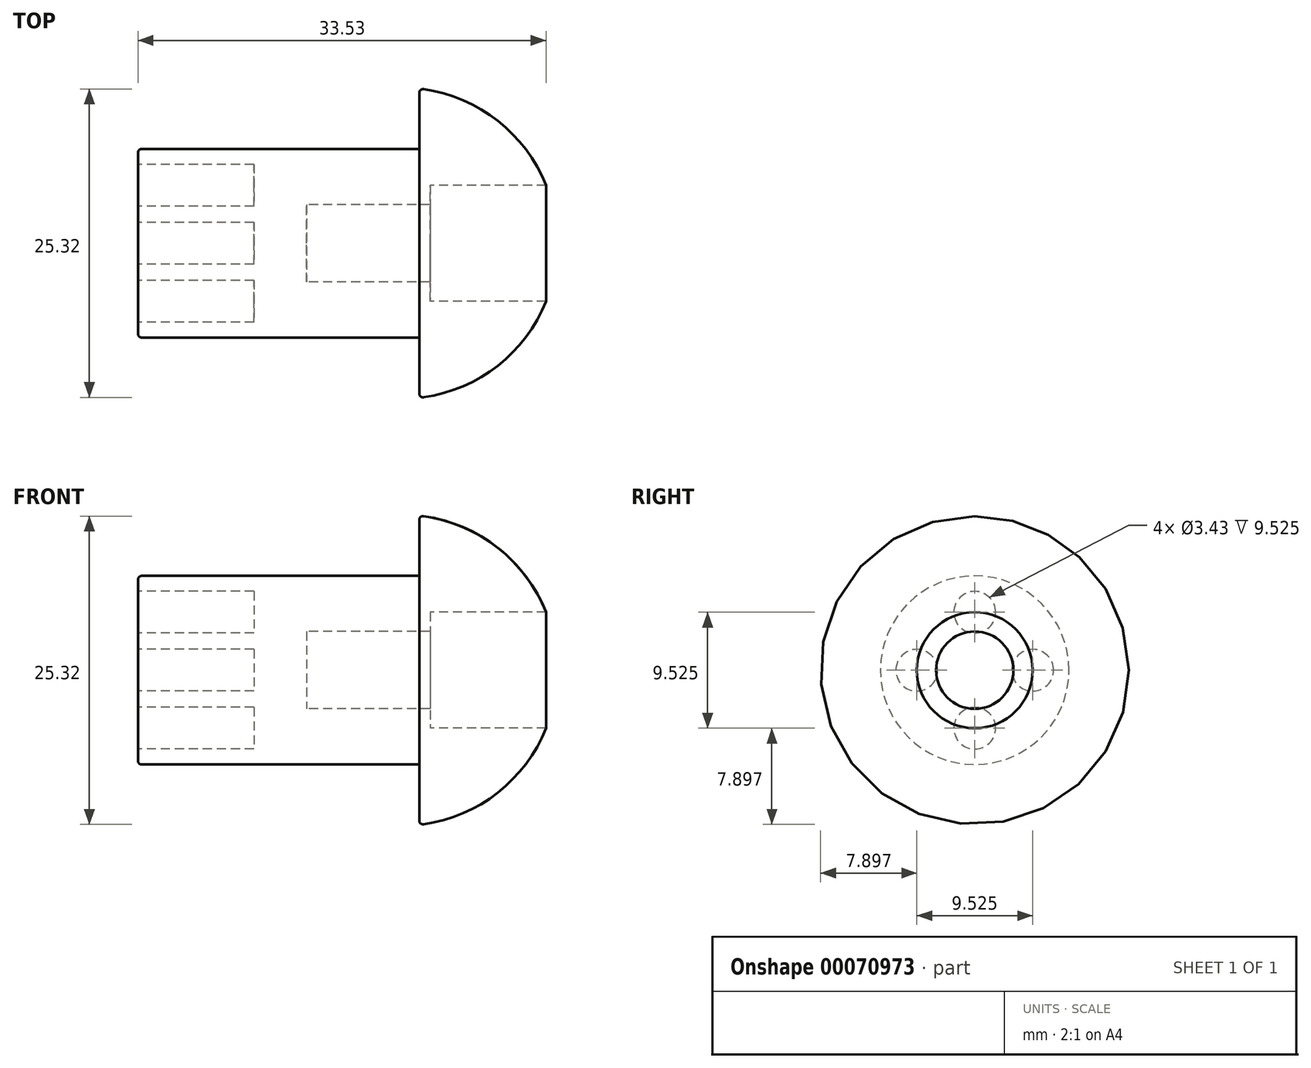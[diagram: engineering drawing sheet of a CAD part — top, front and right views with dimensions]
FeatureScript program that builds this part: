
annotation { "Feature Type Name" : "Feature", "Feature Type Description" : "" }
export const myFeature = defineFeature(function(context is Context, id is Id, definition is map)
    precondition{}
    {
        {
            var Q0;
            Q0=qCreatedBy(makeId("Front.planeOp"),FACE);
            var sketch = newSketch(context, id + "F0", { "sketchPlane" : qUnion([Q0])});
            skLineSegment(sketch, "E0", {"start": v(0, 0) * mm, "end": v(0, 7.75) * mm});
            skLineSegment(sketch, "E1", {"start": v(0, 7.75) * mm, "end": v(23.11, 7.75) * mm});
            skLineSegment(sketch, "E2", {"start": v(23.11, 7.75) * mm, "end": v(23.11, 12.7) * mm});
            skLineSegment(sketch, "E3", {"start": v(0, 0) * mm, "end": v(13.84, 0) * mm});
            skLineSegment(sketch, "E4", {"start": v(33.53, 4.76) * mm, "end": v(24, 4.76) * mm});
            skLineSegment(sketch, "E5", {"start": v(24, 4.76) * mm, "end": v(24, 3.17) * mm});
            skLineSegment(sketch, "E6", {"start": v(24, 3.17) * mm, "end": v(13.84, 3.17) * mm});
            skLineSegment(sketch, "E7", {"start": v(13.84, 3.17) * mm, "end": v(13.84, 0) * mm});
            skArc(sketch, "E8", {"start": v(33.53, 4.76) * mm, "mid": v(29.41, 10.17) * mm, "end": v(23.11, 12.7) * mm});
            skPoint(sketch, "E9.end.orphan", {"position": v(30.27, 12.7) * mm});
            skPoint(sketch, "E10.orphan", {"position": v(33.53, 12.7) * mm});
            skPoint(sketch, "E11.orphan", {"position": v(23.11, 0) * mm});
            skPoint(sketch, "E12.orphan", {"position": v(24, 0) * mm});
            skSolve(sketch);
        }
        {
            var Q0;
            Q0=qSketchRegion(id+"F0",true);
            var Q1;
            Q1=sQuery(id+"F0.wireOp",EDGE,"E3");
            revolve(context, id + "F1", {"entities" : qUnion([Q0]), "axis" : qUnion([Q1]), "revolveType" : RevolveType.FULL});
        }
        {
            var Q0;
            Q0=makeQuery(id+"F1.opRevolve","SWEPT_FACE",FACE,{"disambiguationData":[OSD([sQuery(id+"F0.wireOp",EDGE,"E0")])]});
            var sketch = newSketch(context, id + "F2", { "sketchPlane" : qUnion([Q0])});
            skCircle(sketch, "E13", {"center": v(0, 4.76) * mm, "radius": 1.71 * mm});
            skCircle(sketch, "E14", {"center": v(4.76, 0) * mm, "radius": 1.71 * mm});
            skCircle(sketch, "E15", {"center": v(0, -4.76) * mm, "radius": 1.71 * mm});
            skCircle(sketch, "E16", {"center": v(-4.76, 0) * mm, "radius": 1.71 * mm});
            skSolve(sketch);
        }
        {
            var Q0;
            Q0=qSketchRegion(id+"F2",true);
            extrude(context, id + "F3", {"entities" : qUnion([Q0]), "operationType" : NewBodyOperationType.REMOVE, "oppositeDirection" : true, "depth" : 9.52 * mm});
        }
        {
            var Q0;
            Q0=makeQuery(id+"F1.opRevolve","SWEPT_EDGE",EDGE,{"disambiguationData":[OSD([sQuery(id+"F0.wireOp",EDGE,"E0"),sQuery(id+"F0.wireOp",EDGE,"E1")])]});
            var Q1;
            Q1=makeQuery(id+"F1.opRevolve","SWEPT_EDGE",EDGE,{"disambiguationData":[OSD([sQuery(id+"F0.wireOp",EDGE,"E2"),sQuery(id+"F0.wireOp",EDGE,"E8")])]});
            fillet(context, id + "F4", {"entities" : qUnion([Q0, Q1]), "radius" : 0.3 * mm, "tangentPropagation" : true, "allowEdgeOverflow" : false});
        }
    });
